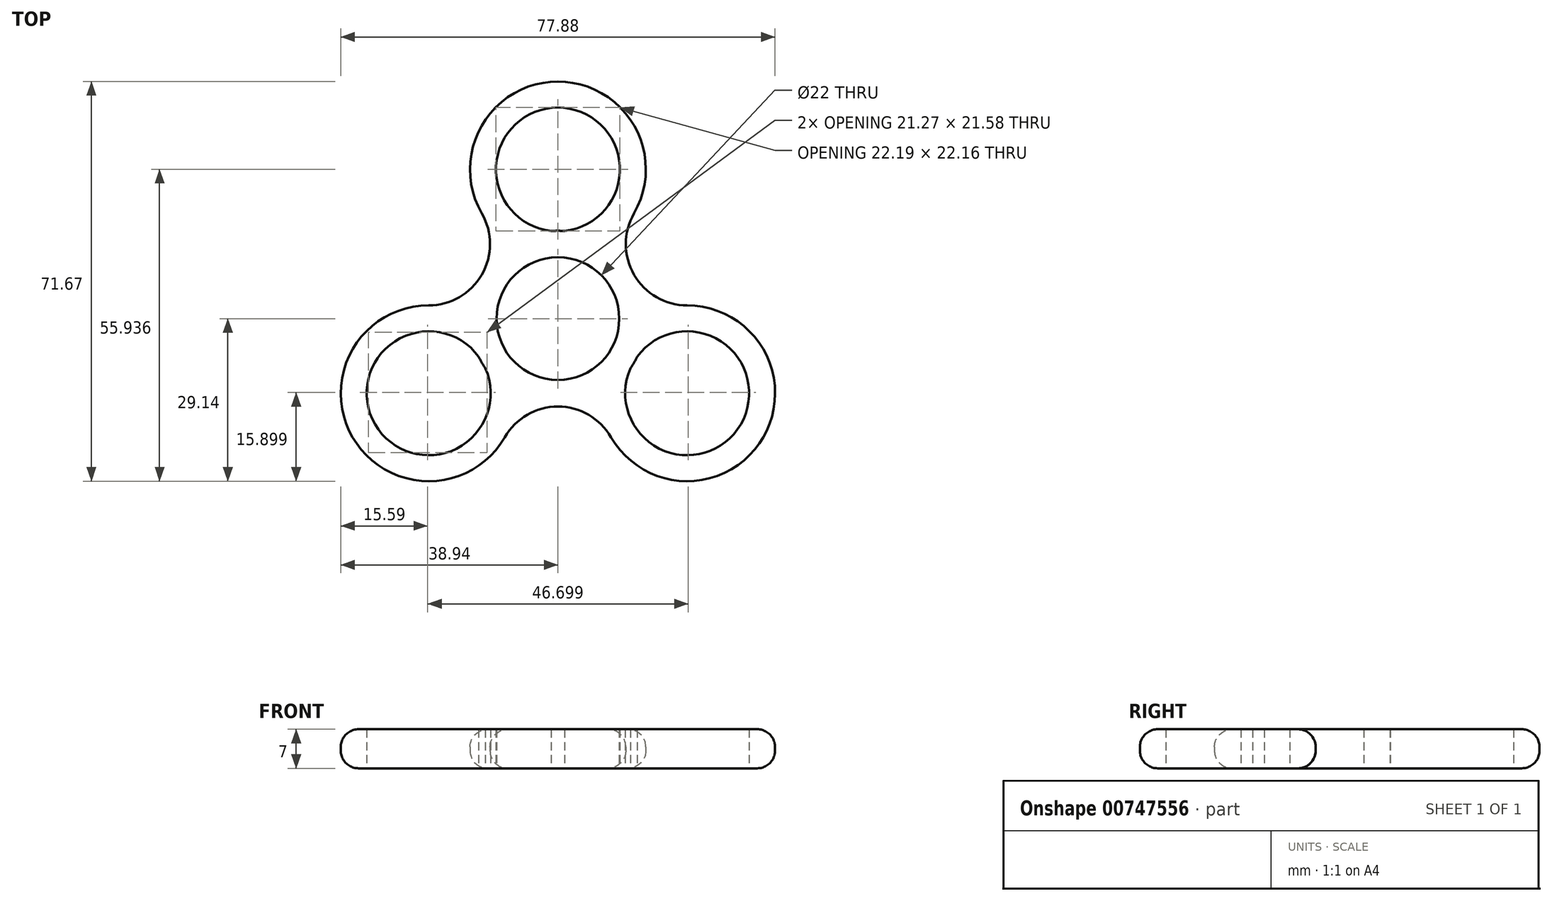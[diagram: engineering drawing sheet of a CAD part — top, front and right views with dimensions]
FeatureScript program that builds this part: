
annotation { "Feature Type Name" : "Feature", "Feature Type Description" : "" }
export const myFeature = defineFeature(function(context is Context, id is Id, definition is map)
    precondition{}
    {
        {
            var Q0;
            Q0=qCreatedBy(makeId("Top.planeOp"),FACE);
            var sketch = newSketch(context, id + "F0", { "sketchPlane" : qUnion([Q0])});
            skCircle(sketch, "E0", {"center": v(0, 0) * mm, "radius": 11 * mm});
            skCircle(sketch, "E1", {"center": v(0, 0) * mm, "radius": 15.76 * mm});
            skLineSegment(sketch, "E2", {"start": v(0, 0) * mm, "end": v(0, 26.76) * mm});
            skCircle(sketch, "E3", {"center": v(0, 26.76) * mm, "radius": 11.11 * mm});
            skArc(sketch, "E4", {"start": v(8.33, 13.38) * mm, "mid": v(0, 42.52) * mm, "end": v(-8.33, 13.38) * mm});
            skLineSegment(sketch, "E5", {"start": v(0, 0) * mm, "end": v(44.23, 25.54) * mm});
            skLineSegment(sketch, "E6", {"start": v(0, 26.76) * mm, "end": v(13.65, 18.88) * mm});
            skLineSegment(sketch, "E7", {"start": v(0, 26.76) * mm, "end": v(-13.65, 18.88) * mm});
            skPoint(sketch, "E8", {"position": v(13.65, 7.88) * mm});
            skArc(sketch, "E9.1.0", {"start": v(-15.75, 0.52) * mm, "mid": v(-36.83, -21.26) * mm, "end": v(-7.42, -13.9) * mm});
            skCircle(sketch, "E9.1.1", {"center": v(-23.18, -13.38) * mm, "radius": 11.11 * mm});
            skLineSegment(sketch, "E9.1.2", {"start": v(-23.18, -13.38) * mm, "end": v(-23.18, 2.38) * mm});
            skLineSegment(sketch, "E9.1.3", {"start": v(-23.18, -13.38) * mm, "end": v(-9.53, -21.26) * mm});
            skLineSegment(sketch, "E9.1.4", {"start": v(0, 0) * mm, "end": v(-23.18, -13.38) * mm});
            skPoint(sketch, "E9.1.5", {"position": v(-13.65, 7.88) * mm});
            skLineSegment(sketch, "E9.1.6", {"start": v(0, 0) * mm, "end": v(-44.23, 25.54) * mm});
            skArc(sketch, "E9.2.0", {"start": v(7.42, -13.9) * mm, "mid": v(36.83, -21.26) * mm, "end": v(15.75, 0.52) * mm});
            skCircle(sketch, "E9.2.1", {"center": v(23.18, -13.38) * mm, "radius": 11.11 * mm});
            skLineSegment(sketch, "E9.2.2", {"start": v(23.18, -13.38) * mm, "end": v(9.53, -21.26) * mm});
            skLineSegment(sketch, "E9.2.3", {"start": v(23.18, -13.38) * mm, "end": v(23.18, 2.38) * mm});
            skLineSegment(sketch, "E9.2.4", {"start": v(0, 0) * mm, "end": v(23.18, -13.38) * mm});
            skPoint(sketch, "E9.2.5", {"position": v(0, -15.76) * mm});
            skLineSegment(sketch, "E9.2.6", {"start": v(0, 0) * mm, "end": v(0, -51.07) * mm});
            skArc(sketch, "E10", {"start": v(13.65, 18.88) * mm, "mid": v(13.65, 7.88) * mm, "end": v(23.18, 2.38) * mm});
            skArc(sketch, "E11", {"start": v(-23.18, 2.38) * mm, "mid": v(-13.65, 7.88) * mm, "end": v(-13.65, 18.88) * mm});
            skArc(sketch, "E12", {"start": v(9.53, -21.26) * mm, "mid": v(0, -15.76) * mm, "end": v(-9.53, -21.26) * mm});
            skSolve(sketch);
        }
        {
            var Q0;
            Q0 = qSketchRegion(id + "F0", true);
            var Q1;
            {var subQ0=sQuery(id+"F0.wireOp",EDGE,"E9.1.3");var subQ1=sQuery(id+"F0.wireOp",EDGE,"E9.1.1");var subQ2=makeQuery(id+"F0.imprint","INTERSECT",VERTEX,{"derivedFrom":[subQ1,subQ0]});Q1=makeQuery(id+"F0.imprint","IMPRINT",FACE,{"disambiguationData":[TD([[makeQuery(id+"F0.imprint","IMPRINT",EDGE,{"disambiguationData":[TD([[subQ2,1.0]])],"derivedFrom":subQ1}),1.0]])]});}
            var Q2;
            {var subQ0=sQuery(id+"F0.wireOp",EDGE,"E9.1.4");var subQ1=sQuery(id+"F0.wireOp",EDGE,"E1");var subQ2=makeQuery(id+"F0.imprint","INTERSECT",VERTEX,{"derivedFrom":[subQ1,subQ0]});Q2=makeQuery(id+"F0.imprint","IMPRINT",FACE,{"disambiguationData":[TD([[makeQuery(id+"F0.imprint","IMPRINT",EDGE,{"disambiguationData":[TD([[subQ2,-1.0]])],"derivedFrom":subQ1}),-1.0]])]});}
            var Q3;
            {var subQ0=sQuery(id+"F0.wireOp",EDGE,"E9.2.3");var subQ1=sQuery(id+"F0.wireOp",EDGE,"E9.2.1");var subQ2=makeQuery(id+"F0.imprint","INTERSECT",VERTEX,{"derivedFrom":[subQ1,subQ0]});Q3=makeQuery(id+"F0.imprint","IMPRINT",FACE,{"disambiguationData":[TD([[makeQuery(id+"F0.imprint","IMPRINT",EDGE,{"disambiguationData":[TD([[subQ2,1.0]])],"derivedFrom":subQ1}),1.0]])]});}
            var Q4;
            {var subQ0=sQuery(id+"F0.wireOp",EDGE,"E9.2.1");var subQ1=sQuery(id+"F0.wireOp",EDGE,"E1");var subQ2=makeQuery(id+"F0.imprint","INTERSECT",VERTEX,{"disambiguationData":[OD(0.0)],"derivedFrom":[subQ1,subQ0]});Q4=makeQuery(id+"F0.imprint","IMPRINT",FACE,{"disambiguationData":[TD([[makeQuery(id+"F0.imprint","IMPRINT",EDGE,{"disambiguationData":[TD([[subQ2,-1.0]])],"derivedFrom":subQ1}),-1.0]])]});}
            var Q5;
            {var subQ0=sQuery(id+"F0.wireOp",EDGE,"E9.2.4");var subQ1=sQuery(id+"F0.wireOp",EDGE,"E1");var subQ2=makeQuery(id+"F0.imprint","INTERSECT",VERTEX,{"derivedFrom":[subQ1,subQ0]});Q5=makeQuery(id+"F0.imprint","IMPRINT",FACE,{"disambiguationData":[TD([[makeQuery(id+"F0.imprint","IMPRINT",EDGE,{"disambiguationData":[TD([[subQ2,-1.0]])],"derivedFrom":subQ1}),-1.0]])]});}
            var Q6;
            {var subQ0=sQuery(id+"F0.wireOp",EDGE,"E9.1.1");var subQ1=sQuery(id+"F0.wireOp",EDGE,"E1");var subQ2=makeQuery(id+"F0.imprint","INTERSECT",VERTEX,{"disambiguationData":[OD(0.0)],"derivedFrom":[subQ1,subQ0]});Q6=makeQuery(id+"F0.imprint","IMPRINT",FACE,{"disambiguationData":[TD([[makeQuery(id+"F0.imprint","IMPRINT",EDGE,{"disambiguationData":[TD([[subQ2,-1.0]])],"derivedFrom":subQ1}),-1.0]])]});}
            var Q7;
            {var subQ0=sQuery(id+"F0.wireOp",EDGE,"E9.2.6");var subQ1=sQuery(id+"F0.wireOp",EDGE,"E0");var subQ2=makeQuery(id+"F0.imprint","INTERSECT",VERTEX,{"derivedFrom":[subQ1,subQ0]});Q7=makeQuery(id+"F0.imprint","IMPRINT",FACE,{"disambiguationData":[TD([[makeQuery(id+"F0.imprint","IMPRINT",EDGE,{"disambiguationData":[TD([[subQ2,-1.0]])],"derivedFrom":subQ1}),1.0]])]});}
            var Q8;
            {var subQ0=sQuery(id+"F0.wireOp",EDGE,"E9.1.4");var subQ1=sQuery(id+"F0.wireOp",EDGE,"E0");var subQ2=makeQuery(id+"F0.imprint","INTERSECT",VERTEX,{"derivedFrom":[subQ1,subQ0]});Q8=makeQuery(id+"F0.imprint","IMPRINT",FACE,{"disambiguationData":[TD([[makeQuery(id+"F0.imprint","IMPRINT",EDGE,{"disambiguationData":[TD([[subQ2,-1.0]])],"derivedFrom":subQ1}),1.0]])]});}
            var Q9;
            {var subQ0=sQuery(id+"F0.wireOp",EDGE,"E9.1.6");var subQ1=sQuery(id+"F0.wireOp",EDGE,"E0");var subQ2=makeQuery(id+"F0.imprint","INTERSECT",VERTEX,{"derivedFrom":[subQ1,subQ0]});Q9=makeQuery(id+"F0.imprint","IMPRINT",FACE,{"disambiguationData":[TD([[makeQuery(id+"F0.imprint","IMPRINT",EDGE,{"disambiguationData":[TD([[subQ2,-1.0]])],"derivedFrom":subQ1}),1.0]])]});}
            var Q10;
            {var subQ0=sQuery(id+"F0.wireOp",EDGE,"E2");var subQ1=sQuery(id+"F0.wireOp",EDGE,"E0");var subQ2=makeQuery(id+"F0.imprint","INTERSECT",VERTEX,{"derivedFrom":[subQ1,subQ0]});Q10=makeQuery(id+"F0.imprint","IMPRINT",FACE,{"disambiguationData":[TD([[makeQuery(id+"F0.imprint","IMPRINT",EDGE,{"disambiguationData":[TD([[subQ2,-1.0]])],"derivedFrom":subQ1}),1.0]])]});}
            var Q11;
            {var subQ0=sQuery(id+"F0.wireOp",EDGE,"E2");var subQ1=sQuery(id+"F0.wireOp",EDGE,"E0");var subQ2=makeQuery(id+"F0.imprint","INTERSECT",VERTEX,{"derivedFrom":[subQ1,subQ0]});Q11=makeQuery(id+"F0.imprint","IMPRINT",FACE,{"disambiguationData":[TD([[makeQuery(id+"F0.imprint","IMPRINT",EDGE,{"disambiguationData":[TD([[subQ2,1.0]])],"derivedFrom":subQ1}),1.0]])]});}
            var Q12;
            {var subQ0=sQuery(id+"F0.wireOp",EDGE,"E5");var subQ1=sQuery(id+"F0.wireOp",EDGE,"E0");var subQ2=makeQuery(id+"F0.imprint","INTERSECT",VERTEX,{"derivedFrom":[subQ1,subQ0]});Q12=makeQuery(id+"F0.imprint","IMPRINT",FACE,{"disambiguationData":[TD([[makeQuery(id+"F0.imprint","IMPRINT",EDGE,{"disambiguationData":[TD([[subQ2,1.0]])],"derivedFrom":subQ1}),1.0]])]});}
            var Q13;
            {var subQ0=sQuery(id+"F0.wireOp",EDGE,"E3");var subQ1=sQuery(id+"F0.wireOp",EDGE,"E1");var subQ2=makeQuery(id+"F0.imprint","INTERSECT",VERTEX,{"disambiguationData":[OD(0.0)],"derivedFrom":[subQ1,subQ0]});Q13=makeQuery(id+"F0.imprint","IMPRINT",FACE,{"disambiguationData":[TD([[makeQuery(id+"F0.imprint","IMPRINT",EDGE,{"disambiguationData":[TD([[subQ2,-1.0]])],"derivedFrom":subQ1}),-1.0]])]});}
            var Q14;
            {var subQ0=sQuery(id+"F0.wireOp",EDGE,"E2");var subQ1=sQuery(id+"F0.wireOp",EDGE,"E1");var subQ2=makeQuery(id+"F0.imprint","INTERSECT",VERTEX,{"derivedFrom":[subQ1,subQ0]});Q14=makeQuery(id+"F0.imprint","IMPRINT",FACE,{"disambiguationData":[TD([[makeQuery(id+"F0.imprint","IMPRINT",EDGE,{"disambiguationData":[TD([[subQ2,-1.0]])],"derivedFrom":subQ1}),-1.0]])]});}
            var Q15;
            {var subQ0=sQuery(id+"F0.wireOp",EDGE,"E7");var subQ1=sQuery(id+"F0.wireOp",EDGE,"E3");var subQ2=makeQuery(id+"F0.imprint","INTERSECT",VERTEX,{"derivedFrom":[subQ1,subQ0]});Q15=makeQuery(id+"F0.imprint","IMPRINT",FACE,{"disambiguationData":[TD([[makeQuery(id+"F0.imprint","IMPRINT",EDGE,{"disambiguationData":[TD([[subQ2,1.0]])],"derivedFrom":subQ1}),1.0]])]});}
            var Q16;
            {var subQ0=sQuery(id+"F0.wireOp",EDGE,"E3");var subQ1=sQuery(id+"F0.wireOp",EDGE,"E1");var subQ2=makeQuery(id+"F0.imprint","INTERSECT",VERTEX,{"disambiguationData":[OD(0.0)],"derivedFrom":[subQ1,subQ0]});Q16=makeQuery(id+"F0.imprint","IMPRINT",FACE,{"disambiguationData":[TD([[makeQuery(id+"F0.imprint","IMPRINT",EDGE,{"disambiguationData":[TD([[subQ2,-1.0]])],"derivedFrom":subQ1}),1.0]])]});}
            var Q17;
            {var subQ0=sQuery(id+"F0.wireOp",EDGE,"E2");var subQ1=sQuery(id+"F0.wireOp",EDGE,"E1");var subQ2=makeQuery(id+"F0.imprint","INTERSECT",VERTEX,{"derivedFrom":[subQ1,subQ0]});Q17=makeQuery(id+"F0.imprint","IMPRINT",FACE,{"disambiguationData":[TD([[makeQuery(id+"F0.imprint","IMPRINT",EDGE,{"disambiguationData":[TD([[subQ2,-1.0]])],"derivedFrom":subQ1}),1.0]])]});}
            var Q18;
            {var subQ0=sQuery(id+"F0.wireOp",EDGE,"E9.1.4");var subQ1=sQuery(id+"F0.wireOp",EDGE,"E1");var subQ2=makeQuery(id+"F0.imprint","INTERSECT",VERTEX,{"derivedFrom":[subQ1,subQ0]});Q18=makeQuery(id+"F0.imprint","IMPRINT",FACE,{"disambiguationData":[TD([[makeQuery(id+"F0.imprint","IMPRINT",EDGE,{"disambiguationData":[TD([[subQ2,-1.0]])],"derivedFrom":subQ1}),1.0]])]});}
            var Q19;
            {var subQ0=sQuery(id+"F0.wireOp",EDGE,"E9.1.1");var subQ1=sQuery(id+"F0.wireOp",EDGE,"E1");var subQ2=makeQuery(id+"F0.imprint","INTERSECT",VERTEX,{"disambiguationData":[OD(0.0)],"derivedFrom":[subQ1,subQ0]});Q19=makeQuery(id+"F0.imprint","IMPRINT",FACE,{"disambiguationData":[TD([[makeQuery(id+"F0.imprint","IMPRINT",EDGE,{"disambiguationData":[TD([[subQ2,-1.0]])],"derivedFrom":subQ1}),1.0]])]});}
            var Q20;
            {var subQ0=sQuery(id+"F0.wireOp",EDGE,"E9.2.4");var subQ1=sQuery(id+"F0.wireOp",EDGE,"E1");var subQ2=makeQuery(id+"F0.imprint","INTERSECT",VERTEX,{"derivedFrom":[subQ1,subQ0]});Q20=makeQuery(id+"F0.imprint","IMPRINT",FACE,{"disambiguationData":[TD([[makeQuery(id+"F0.imprint","IMPRINT",EDGE,{"disambiguationData":[TD([[subQ2,-1.0]])],"derivedFrom":subQ1}),1.0]])]});}
            var Q21;
            {var subQ0=sQuery(id+"F0.wireOp",EDGE,"E9.2.1");var subQ1=sQuery(id+"F0.wireOp",EDGE,"E1");var subQ2=makeQuery(id+"F0.imprint","INTERSECT",VERTEX,{"disambiguationData":[OD(0.0)],"derivedFrom":[subQ1,subQ0]});Q21=makeQuery(id+"F0.imprint","IMPRINT",FACE,{"disambiguationData":[TD([[makeQuery(id+"F0.imprint","IMPRINT",EDGE,{"disambiguationData":[TD([[subQ2,-1.0]])],"derivedFrom":subQ1}),1.0]])]});}
            extrude(context, id + "F1", {"entities" : qUnion([Q0, Q1, Q2, Q3, Q4, Q5, Q6, Q7, Q8, Q9, Q10, Q11, Q12, Q13, Q14, Q15, Q16, Q17, Q18, Q19, Q20, Q21]), "depth" : 7 * mm, "offsetDistance" : 25.4 * mm});
        }
        {
            var Q0;
            Q0=makeQuery(id+"F1.opExtrude","CAP_FACE",FACE,{"disambiguationData":[OSD([sQuery(id+"F0.wireOp",EDGE,"E4"),sQuery(id+"F0.wireOp",EDGE,"E9.1.0"),sQuery(id+"F0.wireOp",EDGE,"E9.2.0"),sQuery(id+"F0.wireOp",EDGE,"E10"),sQuery(id+"F0.wireOp",EDGE,"E11"),sQuery(id+"F0.wireOp",EDGE,"E12")])],"isStart":false});
            var Q1;
            Q1=makeQuery(id+"F1.opExtrude","CAP_FACE",FACE,{"disambiguationData":[OSD([sQuery(id+"F0.wireOp",EDGE,"E4"),sQuery(id+"F0.wireOp",EDGE,"E9.1.0"),sQuery(id+"F0.wireOp",EDGE,"E9.2.0"),sQuery(id+"F0.wireOp",EDGE,"E10"),sQuery(id+"F0.wireOp",EDGE,"E11"),sQuery(id+"F0.wireOp",EDGE,"E12")])],"isStart":true});
            fillet(context, id + "F2", {"entities" : qUnion([Q0, Q1]), "radius" : 3.17 * mm, "tangentPropagation" : true, "allowEdgeOverflow" : false});
        }
        {
            var Q0;
            {var subQ0=sQuery(id+"F0.wireOp",EDGE,"E9.2.4");var subQ1=sQuery(id+"F0.wireOp",EDGE,"E1");var subQ2=makeQuery(id+"F0.imprint","INTERSECT",VERTEX,{"derivedFrom":[subQ1,subQ0]});Q0=makeQuery(id+"F0.imprint","IMPRINT",FACE,{"disambiguationData":[TD([[makeQuery(id+"F0.imprint","IMPRINT",EDGE,{"disambiguationData":[TD([[subQ2,-1.0]])],"derivedFrom":subQ1}),-1.0]])]});}
            var Q1;
            {var subQ0=sQuery(id+"F0.wireOp",EDGE,"E9.2.3");var subQ1=sQuery(id+"F0.wireOp",EDGE,"E9.2.1");var subQ2=makeQuery(id+"F0.imprint","INTERSECT",VERTEX,{"derivedFrom":[subQ1,subQ0]});Q1=makeQuery(id+"F0.imprint","IMPRINT",FACE,{"disambiguationData":[TD([[makeQuery(id+"F0.imprint","IMPRINT",EDGE,{"disambiguationData":[TD([[subQ2,1.0]])],"derivedFrom":subQ1}),1.0]])]});}
            var Q2;
            {var subQ0=sQuery(id+"F0.wireOp",EDGE,"E9.2.1");var subQ1=sQuery(id+"F0.wireOp",EDGE,"E1");var subQ2=makeQuery(id+"F0.imprint","INTERSECT",VERTEX,{"disambiguationData":[OD(0.0)],"derivedFrom":[subQ1,subQ0]});Q2=makeQuery(id+"F0.imprint","IMPRINT",FACE,{"disambiguationData":[TD([[makeQuery(id+"F0.imprint","IMPRINT",EDGE,{"disambiguationData":[TD([[subQ2,-1.0]])],"derivedFrom":subQ1}),-1.0]])]});}
            var Q3;
            {var subQ0=sQuery(id+"F0.wireOp",EDGE,"E5");var subQ1=sQuery(id+"F0.wireOp",EDGE,"E0");var subQ2=makeQuery(id+"F0.imprint","INTERSECT",VERTEX,{"derivedFrom":[subQ1,subQ0]});Q3=makeQuery(id+"F0.imprint","IMPRINT",FACE,{"disambiguationData":[TD([[makeQuery(id+"F0.imprint","IMPRINT",EDGE,{"disambiguationData":[TD([[subQ2,1.0]])],"derivedFrom":subQ1}),1.0]])]});}
            var Q4;
            {var subQ0=sQuery(id+"F0.wireOp",EDGE,"E2");var subQ1=sQuery(id+"F0.wireOp",EDGE,"E0");var subQ2=makeQuery(id+"F0.imprint","INTERSECT",VERTEX,{"derivedFrom":[subQ1,subQ0]});Q4=makeQuery(id+"F0.imprint","IMPRINT",FACE,{"disambiguationData":[TD([[makeQuery(id+"F0.imprint","IMPRINT",EDGE,{"disambiguationData":[TD([[subQ2,-1.0]])],"derivedFrom":subQ1}),1.0]])]});}
            var Q5;
            {var subQ0=sQuery(id+"F0.wireOp",EDGE,"E2");var subQ1=sQuery(id+"F0.wireOp",EDGE,"E0");var subQ2=makeQuery(id+"F0.imprint","INTERSECT",VERTEX,{"derivedFrom":[subQ1,subQ0]});Q5=makeQuery(id+"F0.imprint","IMPRINT",FACE,{"disambiguationData":[TD([[makeQuery(id+"F0.imprint","IMPRINT",EDGE,{"disambiguationData":[TD([[subQ2,1.0]])],"derivedFrom":subQ1}),1.0]])]});}
            var Q6;
            {var subQ0=sQuery(id+"F0.wireOp",EDGE,"E9.2.6");var subQ1=sQuery(id+"F0.wireOp",EDGE,"E0");var subQ2=makeQuery(id+"F0.imprint","INTERSECT",VERTEX,{"derivedFrom":[subQ1,subQ0]});Q6=makeQuery(id+"F0.imprint","IMPRINT",FACE,{"disambiguationData":[TD([[makeQuery(id+"F0.imprint","IMPRINT",EDGE,{"disambiguationData":[TD([[subQ2,-1.0]])],"derivedFrom":subQ1}),1.0]])]});}
            var Q7;
            {var subQ0=sQuery(id+"F0.wireOp",EDGE,"E9.1.4");var subQ1=sQuery(id+"F0.wireOp",EDGE,"E0");var subQ2=makeQuery(id+"F0.imprint","INTERSECT",VERTEX,{"derivedFrom":[subQ1,subQ0]});Q7=makeQuery(id+"F0.imprint","IMPRINT",FACE,{"disambiguationData":[TD([[makeQuery(id+"F0.imprint","IMPRINT",EDGE,{"disambiguationData":[TD([[subQ2,-1.0]])],"derivedFrom":subQ1}),1.0]])]});}
            var Q8;
            {var subQ0=sQuery(id+"F0.wireOp",EDGE,"E9.1.6");var subQ1=sQuery(id+"F0.wireOp",EDGE,"E0");var subQ2=makeQuery(id+"F0.imprint","INTERSECT",VERTEX,{"derivedFrom":[subQ1,subQ0]});Q8=makeQuery(id+"F0.imprint","IMPRINT",FACE,{"disambiguationData":[TD([[makeQuery(id+"F0.imprint","IMPRINT",EDGE,{"disambiguationData":[TD([[subQ2,-1.0]])],"derivedFrom":subQ1}),1.0]])]});}
            var Q9;
            {var subQ0=sQuery(id+"F0.wireOp",EDGE,"E9.1.1");var subQ1=sQuery(id+"F0.wireOp",EDGE,"E1");var subQ2=makeQuery(id+"F0.imprint","INTERSECT",VERTEX,{"disambiguationData":[OD(0.0)],"derivedFrom":[subQ1,subQ0]});Q9=makeQuery(id+"F0.imprint","IMPRINT",FACE,{"disambiguationData":[TD([[makeQuery(id+"F0.imprint","IMPRINT",EDGE,{"disambiguationData":[TD([[subQ2,-1.0]])],"derivedFrom":subQ1}),-1.0]])]});}
            var Q10;
            {var subQ0=sQuery(id+"F0.wireOp",EDGE,"E9.1.4");var subQ1=sQuery(id+"F0.wireOp",EDGE,"E1");var subQ2=makeQuery(id+"F0.imprint","INTERSECT",VERTEX,{"derivedFrom":[subQ1,subQ0]});Q10=makeQuery(id+"F0.imprint","IMPRINT",FACE,{"disambiguationData":[TD([[makeQuery(id+"F0.imprint","IMPRINT",EDGE,{"disambiguationData":[TD([[subQ2,-1.0]])],"derivedFrom":subQ1}),-1.0]])]});}
            var Q11;
            {var subQ0=sQuery(id+"F0.wireOp",EDGE,"E9.1.3");var subQ1=sQuery(id+"F0.wireOp",EDGE,"E9.1.1");var subQ2=makeQuery(id+"F0.imprint","INTERSECT",VERTEX,{"derivedFrom":[subQ1,subQ0]});Q11=makeQuery(id+"F0.imprint","IMPRINT",FACE,{"disambiguationData":[TD([[makeQuery(id+"F0.imprint","IMPRINT",EDGE,{"disambiguationData":[TD([[subQ2,1.0]])],"derivedFrom":subQ1}),1.0]])]});}
            var Q12;
            {var subQ0=sQuery(id+"F0.wireOp",EDGE,"E3");var subQ1=sQuery(id+"F0.wireOp",EDGE,"E1");var subQ2=makeQuery(id+"F0.imprint","INTERSECT",VERTEX,{"disambiguationData":[OD(0.0)],"derivedFrom":[subQ1,subQ0]});Q12=makeQuery(id+"F0.imprint","IMPRINT",FACE,{"disambiguationData":[TD([[makeQuery(id+"F0.imprint","IMPRINT",EDGE,{"disambiguationData":[TD([[subQ2,-1.0]])],"derivedFrom":subQ1}),-1.0]])]});}
            var Q13;
            {var subQ0=sQuery(id+"F0.wireOp",EDGE,"E2");var subQ1=sQuery(id+"F0.wireOp",EDGE,"E1");var subQ2=makeQuery(id+"F0.imprint","INTERSECT",VERTEX,{"derivedFrom":[subQ1,subQ0]});Q13=makeQuery(id+"F0.imprint","IMPRINT",FACE,{"disambiguationData":[TD([[makeQuery(id+"F0.imprint","IMPRINT",EDGE,{"disambiguationData":[TD([[subQ2,-1.0]])],"derivedFrom":subQ1}),-1.0]])]});}
            var Q14;
            {var subQ0=sQuery(id+"F0.wireOp",EDGE,"E7");var subQ1=sQuery(id+"F0.wireOp",EDGE,"E3");var subQ2=makeQuery(id+"F0.imprint","INTERSECT",VERTEX,{"derivedFrom":[subQ1,subQ0]});Q14=makeQuery(id+"F0.imprint","IMPRINT",FACE,{"disambiguationData":[TD([[makeQuery(id+"F0.imprint","IMPRINT",EDGE,{"disambiguationData":[TD([[subQ2,1.0]])],"derivedFrom":subQ1}),1.0]])]});}
            extrude(context, id + "F3", {"entities" : qUnion([Q0, Q1, Q2, Q3, Q4, Q5, Q6, Q7, Q8, Q9, Q10, Q11, Q12, Q13, Q14]), "operationType" : NewBodyOperationType.REMOVE, "endBound" : BoundingType.THROUGH_ALL, "depth" : 25.4 * mm, "offsetDistance" : 25.4 * mm});
        }
    });
